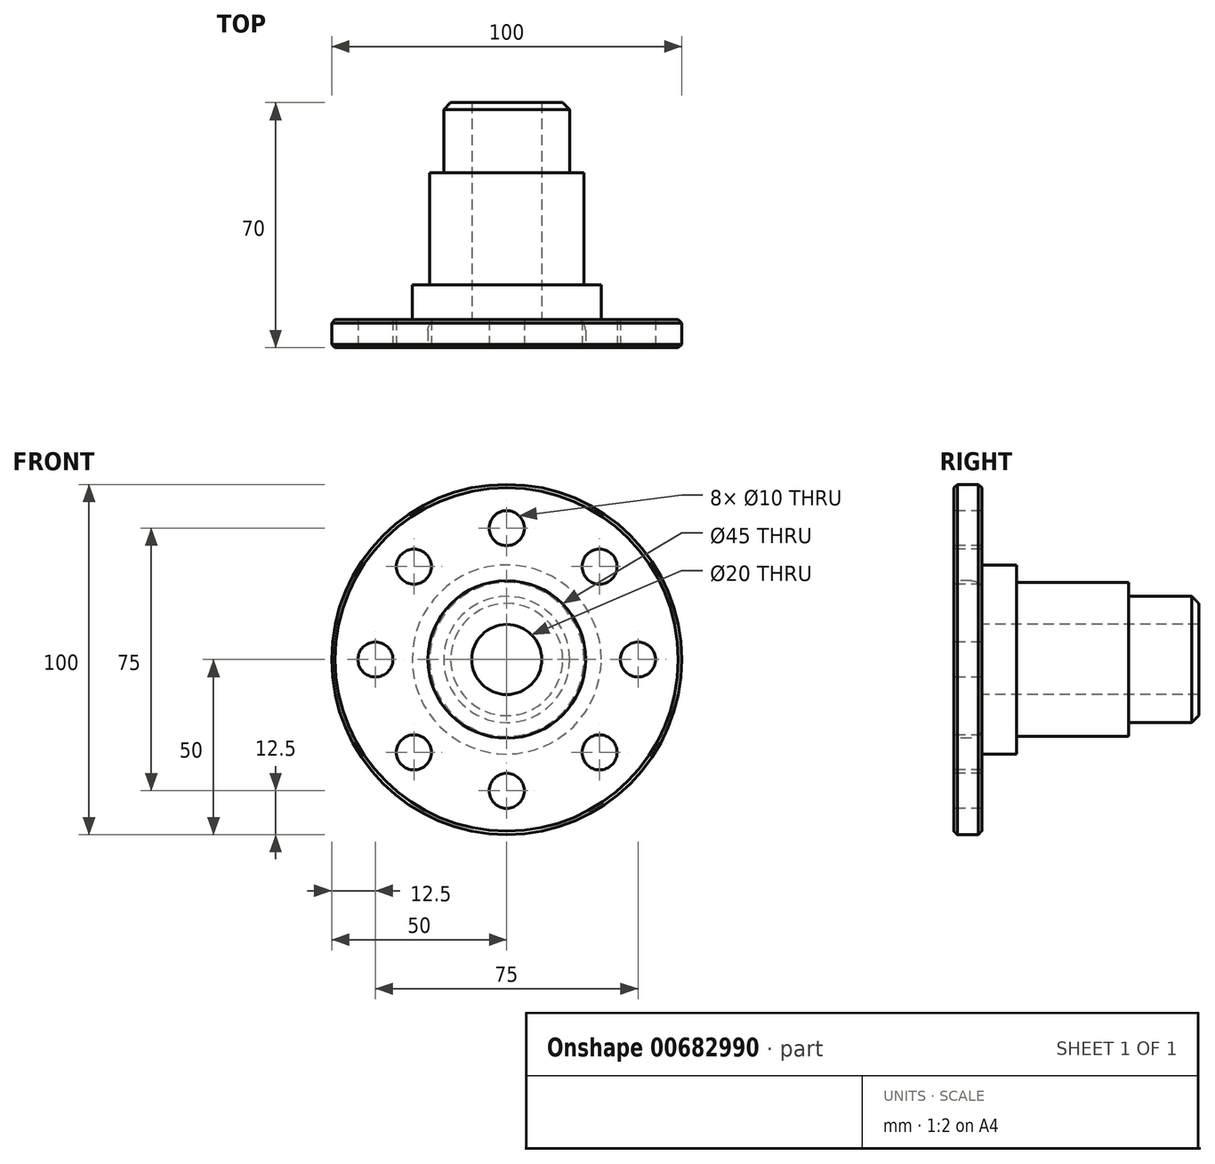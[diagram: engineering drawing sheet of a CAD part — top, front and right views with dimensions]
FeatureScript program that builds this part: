
annotation { "Feature Type Name" : "Feature", "Feature Type Description" : "" }
export const myFeature = defineFeature(function(context is Context, id is Id, definition is map)
    precondition{}
    {
        {
            var Q0;
            Q0=qCreatedBy(makeId("Front.planeOp"),FACE);
            var sketch = newSketch(context, id + "F0", { "sketchPlane" : qUnion([Q0])});
            skCircle(sketch, "E0", {"center": v(0, 0) * mm, "radius": 50 * mm});
            skCircle(sketch, "E1", {"center": v(0, 37.5) * mm, "radius": 5 * mm});
            skCircle(sketch, "E2.1.0", {"center": v(-26.52, 26.52) * mm, "radius": 5 * mm});
            skCircle(sketch, "E2.2.0", {"center": v(-37.5, 0) * mm, "radius": 5 * mm});
            skCircle(sketch, "E2.3.0", {"center": v(-26.52, -26.52) * mm, "radius": 5 * mm});
            skCircle(sketch, "E2.4.0", {"center": v(0, -37.5) * mm, "radius": 5 * mm});
            skCircle(sketch, "E2.5.0", {"center": v(26.52, -26.52) * mm, "radius": 5 * mm});
            skCircle(sketch, "E2.6.0", {"center": v(37.5, 0) * mm, "radius": 5 * mm});
            skCircle(sketch, "E2.7.0", {"center": v(26.52, 26.52) * mm, "radius": 5 * mm});
            skSolve(sketch);
        }
        {
            var Q0;
            Q0 = qSketchRegion(id + "F0", true);
            extrude(context, id + "F1", {"entities" : qUnion([Q0]), "oppositeDirection" : true, "depth" : 8 * mm, "offsetDistance" : 25 * mm});
        }
        {
            var Q0;
            Q0=makeQuery(id+"F1.opExtrude","CAP_FACE",FACE,{"disambiguationData":[OSD([sQuery(id+"F0.wireOp",EDGE,"E0"),sQuery(id+"F0.wireOp",EDGE,"E1"),sQuery(id+"F0.wireOp",EDGE,"E2.1.0"),sQuery(id+"F0.wireOp",EDGE,"E2.2.0"),sQuery(id+"F0.wireOp",EDGE,"E2.3.0"),sQuery(id+"F0.wireOp",EDGE,"E2.4.0"),sQuery(id+"F0.wireOp",EDGE,"E2.5.0"),sQuery(id+"F0.wireOp",EDGE,"E2.6.0"),sQuery(id+"F0.wireOp",EDGE,"E2.7.0")])],"isStart":false});
            var sketch = newSketch(context, id + "F2", { "sketchPlane" : qUnion([Q0])});
            skCircle(sketch, "E3", {"center": v(0, 0) * mm, "radius": 27 * mm});
            skSolve(sketch);
        }
        {
            var Q0;
            Q0 = qSketchRegion(id + "F2", true);
            extrude(context, id + "F3", {"entities" : qUnion([Q0]), "operationType" : NewBodyOperationType.ADD, "depth" : 10 * mm, "offsetDistance" : 25 * mm});
        }
        {
            var Q0;
            Q0=makeQuery(id+"F3.opExtrude","CAP_FACE",FACE,{"disambiguationData":[OSD([sQuery(id+"F2.wireOp",EDGE,"E3")])],"isStart":false});
            var sketch = newSketch(context, id + "F4", { "sketchPlane" : qUnion([Q0])});
            skCircle(sketch, "E4", {"center": v(0, 0) * mm, "radius": 22 * mm});
            skSolve(sketch);
        }
        {
            var Q0;
            Q0=makeQuery(id+"F4.imprint","IMPRINT",FACE,{"disambiguationData":[TD([[makeQuery(id+"F4.imprint","IMPRINT",EDGE,{"derivedFrom":sQuery(id+"F4.wireOp",EDGE,"E4")}),1.0]])]});
            extrude(context, id + "F5", {"entities" : qUnion([Q0]), "operationType" : NewBodyOperationType.ADD, "depth" : 32 * mm, "offsetDistance" : 25 * mm});
        }
        {
            var Q0;
            Q0=makeQuery(id+"F5.opExtrude","CAP_FACE",FACE,{"disambiguationData":[OSD([sQuery(id+"F4.wireOp",EDGE,"E4")])],"isStart":false});
            var sketch = newSketch(context, id + "F6", { "sketchPlane" : qUnion([Q0])});
            skCircle(sketch, "E5", {"center": v(0, 0) * mm, "radius": 18 * mm});
            skSolve(sketch);
        }
        {
            var Q0;
            Q0 = qSketchRegion(id + "F6", true);
            extrude(context, id + "F7", {"entities" : qUnion([Q0]), "operationType" : NewBodyOperationType.ADD, "depth" : 20 * mm, "offsetDistance" : 25 * mm});
        }
        {
            var Q0;
            Q0=makeQuery(id+"F1.opExtrude","CAP_FACE",FACE,{"disambiguationData":[OSD([sQuery(id+"F0.wireOp",EDGE,"E0"),sQuery(id+"F0.wireOp",EDGE,"E1"),sQuery(id+"F0.wireOp",EDGE,"E2.1.0"),sQuery(id+"F0.wireOp",EDGE,"E2.2.0"),sQuery(id+"F0.wireOp",EDGE,"E2.3.0"),sQuery(id+"F0.wireOp",EDGE,"E2.4.0"),sQuery(id+"F0.wireOp",EDGE,"E2.5.0"),sQuery(id+"F0.wireOp",EDGE,"E2.6.0"),sQuery(id+"F0.wireOp",EDGE,"E2.7.0")])],"isStart":true});
            var sketch = newSketch(context, id + "F8", { "sketchPlane" : qUnion([Q0])});
            skCircle(sketch, "E6", {"center": v(0, 0) * mm, "radius": 22.5 * mm});
            skSolve(sketch);
        }
        {
            var Q0;
            Q0 = qSketchRegion(id + "F8", true);
            extrude(context, id + "F9", {"entities" : qUnion([Q0]), "operationType" : NewBodyOperationType.REMOVE, "oppositeDirection" : true, "depth" : 8 * mm, "offsetDistance" : 25 * mm});
        }
        {
            var Q0;
            Q0=makeQuery(id+"F9.boolean.opBoolean","COPY",FACE,{"derivedFrom":makeQuery(id+"F9.opExtrude","CAP_FACE",FACE,{"disambiguationData":[OSD([sQuery(id+"F8.wireOp",EDGE,"E6")])],"isStart":false})});
            var sketch = newSketch(context, id + "F10", { "sketchPlane" : qUnion([Q0])});
            skPoint(sketch, "E7", {"position": v(0, 0) * mm});
            skSolve(sketch);
        }
        {
            var Q0;
            Q0=sQuery(id+"F10.wireOp",VERTEX,"E7");
            var Q1;
            Q1=makeQuery(id+"F1.opExtrude","SWEPT_BODY",BODY,{"disambiguationData":[OSD([sQuery(id+"F0.wireOp",EDGE,"E0"),sQuery(id+"F0.wireOp",EDGE,"E1"),sQuery(id+"F0.wireOp",EDGE,"E2.1.0"),sQuery(id+"F0.wireOp",EDGE,"E2.2.0"),sQuery(id+"F0.wireOp",EDGE,"E2.3.0"),sQuery(id+"F0.wireOp",EDGE,"E2.4.0"),sQuery(id+"F0.wireOp",EDGE,"E2.5.0"),sQuery(id+"F0.wireOp",EDGE,"E2.6.0"),sQuery(id+"F0.wireOp",EDGE,"E2.7.0")])]});
            hole(context, id + "F11", {"style" : HoleStyle.SIMPLE, "endStyle" : HoleEndStyle.THROUGH, "holeDiameter" : 20 * mm, "majorDiameter" : 5 * mm, "isTappedThrough" : true, "tappedDepth" : 12 * mm, "tapClearance" : 0, "locations" : qUnion([Q0]), "scope" : qUnion([Q1])});
        }
        {
            var Q0;
            Q0=makeQuery(id+"F9.boolean.opBoolean","COPY",EDGE,{"derivedFrom":makeQuery(id+"F9.opExtrude","CAP_EDGE",EDGE,{"disambiguationData":[OSD([sQuery(id+"F8.wireOp",EDGE,"E6")])],"isStart":true})});
            var Q1;
            Q1=makeQuery(id+"F11.hole-0.boolean.opBoolean","COPY",EDGE,{"derivedFrom":makeQuery(id+"F11.hole-0.opRevolve","SWEPT_EDGE",EDGE,{"disambiguationData":[OSD([sQuery(id+"F11.hole-0.sketch.wireOp",EDGE,"cbore_start_line_2"),sQuery(id+"F11.hole-0.sketch.wireOp",EDGE,"cbore_start_line_3")])]})});
            var Q2;
            Q2=makeQuery(id+"F7.opExtrude","CAP_EDGE",EDGE,{"disambiguationData":[OSD([sQuery(id+"F6.wireOp",EDGE,"E5")])],"isStart":false});
            chamfer(context, id + "F12", {"entities" : qUnion([Q0, Q1, Q2]), "width" : 2 * mm, "tangentPropagation" : true});
        }
        {
            var Q0;
            Q0=makeQuery(id+"F9.boolean.opBoolean","COPY",EDGE,{"derivedFrom":makeQuery(id+"F9.opExtrude","CAP_EDGE",EDGE,{"disambiguationData":[OSD([sQuery(id+"F8.wireOp",EDGE,"E6")])],"isStart":false})});
            var Q1;
            Q1=makeQuery(id+"F5.opExtrude","CAP_EDGE",EDGE,{"disambiguationData":[OSD([sQuery(id+"F4.wireOp",EDGE,"E4")])],"isStart":true});
            var Q2;
            Q2=makeQuery(id+"F7.opExtrude","CAP_EDGE",EDGE,{"disambiguationData":[OSD([sQuery(id+"F6.wireOp",EDGE,"E5")])],"isStart":true});
            fillet(context, id + "F13", {"entities" : qUnion([Q0, Q1, Q2]), "radius" : 3 * mm, "tangentPropagation" : true, "allowEdgeOverflow" : false});
        }
        {
            var Q0;
            Q0=makeQuery(id+"F1.opExtrude","CAP_EDGE",EDGE,{"disambiguationData":[OSD([sQuery(id+"F0.wireOp",EDGE,"E0")])],"isStart":true});
            var Q1;
            Q1=makeQuery(id+"F1.opExtrude","CAP_EDGE",EDGE,{"disambiguationData":[OSD([sQuery(id+"F0.wireOp",EDGE,"E0")])],"isStart":false});
            chamfer(context, id + "F14", {"entities" : qUnion([Q0, Q1]), "width" : 1 * mm, "tangentPropagation" : true});
        }
    });
